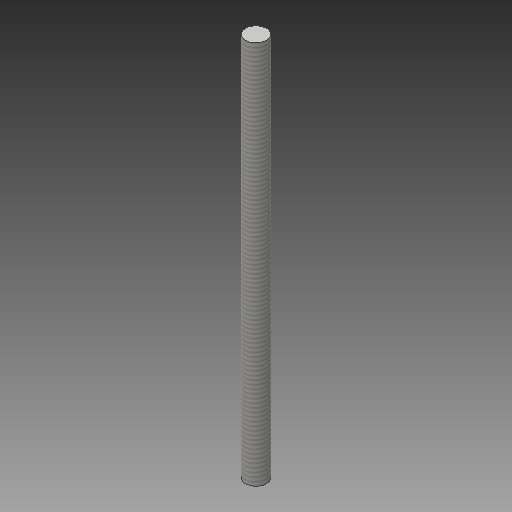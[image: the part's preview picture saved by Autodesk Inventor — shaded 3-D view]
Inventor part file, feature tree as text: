
AUTODESK INVENTOR PART (.ipt)
format: ipt  version: 2017 (Build 210142000, 142)  size: 96,256 bytes
history: native  units: in
note: dims shown in document units (in); Inventor stores cm internally (conversion verified against a paired STEP export)
features: extrude x1, thread x1, sketch x1
ambient origin geometry x8: Origin, YZ Plane, XZ Plane, XY Plane, X Axis, Y Axis, Z Axis, Center Point
bodies: Solid1 (feature_tree)
feature tree (3):
  extrude  "Extrusion1"  Depth=3.0in TaperAngle=0.0deg
  thread  "Thread1"  [1 undecoded]
  sketch  "Sketch1"  dims[d0=0.164in d1=3.0in d2=0.0in d3=1.0in d4=0.0in]
note: 1 required parameter value undecoded (feature->parameter linkage not recoverable at this tier; creation-order binding heuristic only, values carry confidence <= 0.55)
